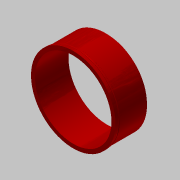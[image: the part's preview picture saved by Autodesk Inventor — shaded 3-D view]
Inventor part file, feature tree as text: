
AUTODESK INVENTOR PART (.ipt)
format: ipt  version: 2017.3 (Build 213257000, 257)  size: 208,896 bytes
history: native  units: in
note: dims shown in document units (in); Inventor stores cm internally (conversion verified against a paired STEP export)
features: extrude x4, sketch x4, chamfer x3, fillet x1, revolve x1
ambient origin geometry x8: Origin, YZ Plane, XZ Plane, XY Plane, X Axis, Y Axis, Z Axis, Center Point
bodies: Solid1 (feature_tree)
feature tree (13):
  extrude  "Extrusion1"  Depth=31.0in
  sketch  "Sketch2"  dims[d2=12.0in d3=0.0in d4=31.23in]
  extrude  "Extrusion2"  Depth=12.0in
  extrude  "Extrusion3"  Depth=1.0in TaperAngle=0.0deg
  chamfer  "Chamfer1"  Distance=1.0in
  extrude  "Extrusion4"  Depth=0.1875in TaperAngle=45.0deg
  fillet  "Fillet1"  Radius=29.98in
  chamfer  "Chamfer2"  Distance=0.5in
  chamfer  "Chamfer3"  Distance=0.0312in
  revolve  "Revolution1"  Angle=45.0deg
  sketch  "Sketch1"  dims[d0=28.5in d1=31.0in]
  sketch  "Sketch3"  dims[d5=31.48in d6=2.0in d7=0.0in d8=1.0in d9=0.0in]
  sketch  "Sketch4"  dims[d10=0.115in d11=0.125in d12=45.0deg d13=29.98in d14=0.5in d15=0.0in d16=0.0312in d17=0.0312in d18=0.125in d19=45.0deg d20=0.0312in d21=0.125in d22=45.0deg d23=0.4375in d24=0.125in d25=0.1875in d26=1.25in d27=45.0deg d28=90.0deg]
